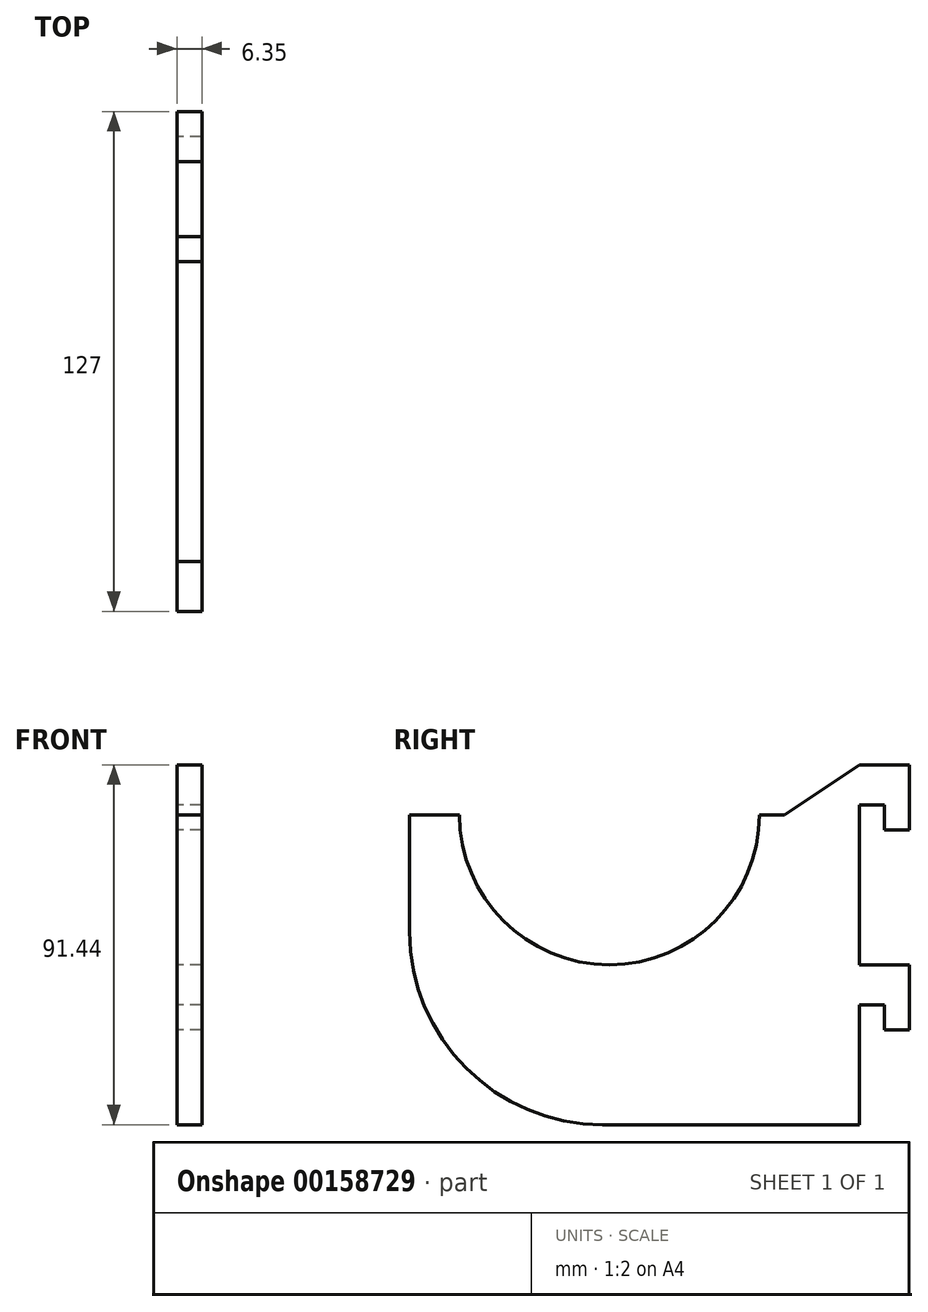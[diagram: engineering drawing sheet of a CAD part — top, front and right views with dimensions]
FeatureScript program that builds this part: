
annotation { "Feature Type Name" : "Feature", "Feature Type Description" : "" }
export const myFeature = defineFeature(function(context is Context, id is Id, definition is map)
    precondition{}
    {
        {
            var Q0;
            Q0=qCreatedBy(makeId("Right.planeOp"),FACE);
            var sketch = newSketch(context, id + "F0", { "sketchPlane" : qUnion([Q0])});
            skLineSegment(sketch, "E0", {"start": v(-19.05, 0) * mm, "end": v(-25.4, 0) * mm});
            skLineSegment(sketch, "E1", {"start": v(-114.3, 0) * mm, "end": v(-114.3, -78.74) * mm});
            skLineSegment(sketch, "E2", {"start": v(-114.3, -78.74) * mm, "end": v(0, -78.74) * mm});
            skLineSegment(sketch, "E3", {"start": v(0, -78.74) * mm, "end": v(0, -48.26) * mm});
            skArc(sketch, "E4", {"start": v(-101.6, 0) * mm, "mid": v(-63.5, -38.1) * mm, "end": v(-25.4, 0) * mm});
            skLineSegment(sketch, "E5.trimOffspring", {"start": v(-101.6, 0) * mm, "end": v(-114.3, 0) * mm});
            skLineSegment(sketch, "E6", {"start": v(-19.05, 0) * mm, "end": v(0, 12.7) * mm});
            skLineSegment(sketch, "E7", {"start": v(0, 12.7) * mm, "end": v(12.7, 12.7) * mm});
            skLineSegment(sketch, "E8", {"start": v(12.7, 12.7) * mm, "end": v(12.7, -3.8) * mm});
            skLineSegment(sketch, "E9", {"start": v(12.7, -3.8) * mm, "end": v(6.35, -3.8) * mm});
            skLineSegment(sketch, "E10", {"start": v(6.35, -3.8) * mm, "end": v(6.35, 2.54) * mm});
            skLineSegment(sketch, "E11", {"start": v(6.35, 2.54) * mm, "end": v(0, 2.54) * mm});
            skLineSegment(sketch, "E12", {"start": v(0, -38.1) * mm, "end": v(12.7, -38.1) * mm});
            skLineSegment(sketch, "E13", {"start": v(12.7, -38.1) * mm, "end": v(12.7, -54.6) * mm});
            skLineSegment(sketch, "E14", {"start": v(12.7, -54.6) * mm, "end": v(6.35, -54.6) * mm});
            skLineSegment(sketch, "E15", {"start": v(6.35, -54.6) * mm, "end": v(6.35, -48.26) * mm});
            skLineSegment(sketch, "E16", {"start": v(6.35, -48.26) * mm, "end": v(0, -48.26) * mm});
            skLineSegment(sketch, "E17.trimOffspring", {"start": v(0, -38.1) * mm, "end": v(0, 2.54) * mm});
            skSolve(sketch);
        }
        {
            var Q0;
            Q0=makeQuery(id+"F0.imprint","IMPRINT",FACE,{"disambiguationData":[TD([[makeQuery(id+"F0.imprint","IMPRINT",EDGE,{"derivedFrom":sQuery(id+"F0.wireOp",EDGE,"E0")}),1.0]])]});
            extrude(context, id + "F1", {"entities" : qUnion([Q0]), "depth" : 6.35 * mm});
        }
        {
            var Q0;
            Q0=makeQuery(id+"F1.opExtrude","SWEPT_EDGE",EDGE,{"disambiguationData":[OSD([sQuery(id+"F0.wireOp",EDGE,"E1"),sQuery(id+"F0.wireOp",EDGE,"E2")])]});
            fillet(context, id + "F2", {"entities" : qUnion([Q0]), "radius" : 49.06 * mm, "tangentPropagation" : true, "allowEdgeOverflow" : false});
        }
    });
